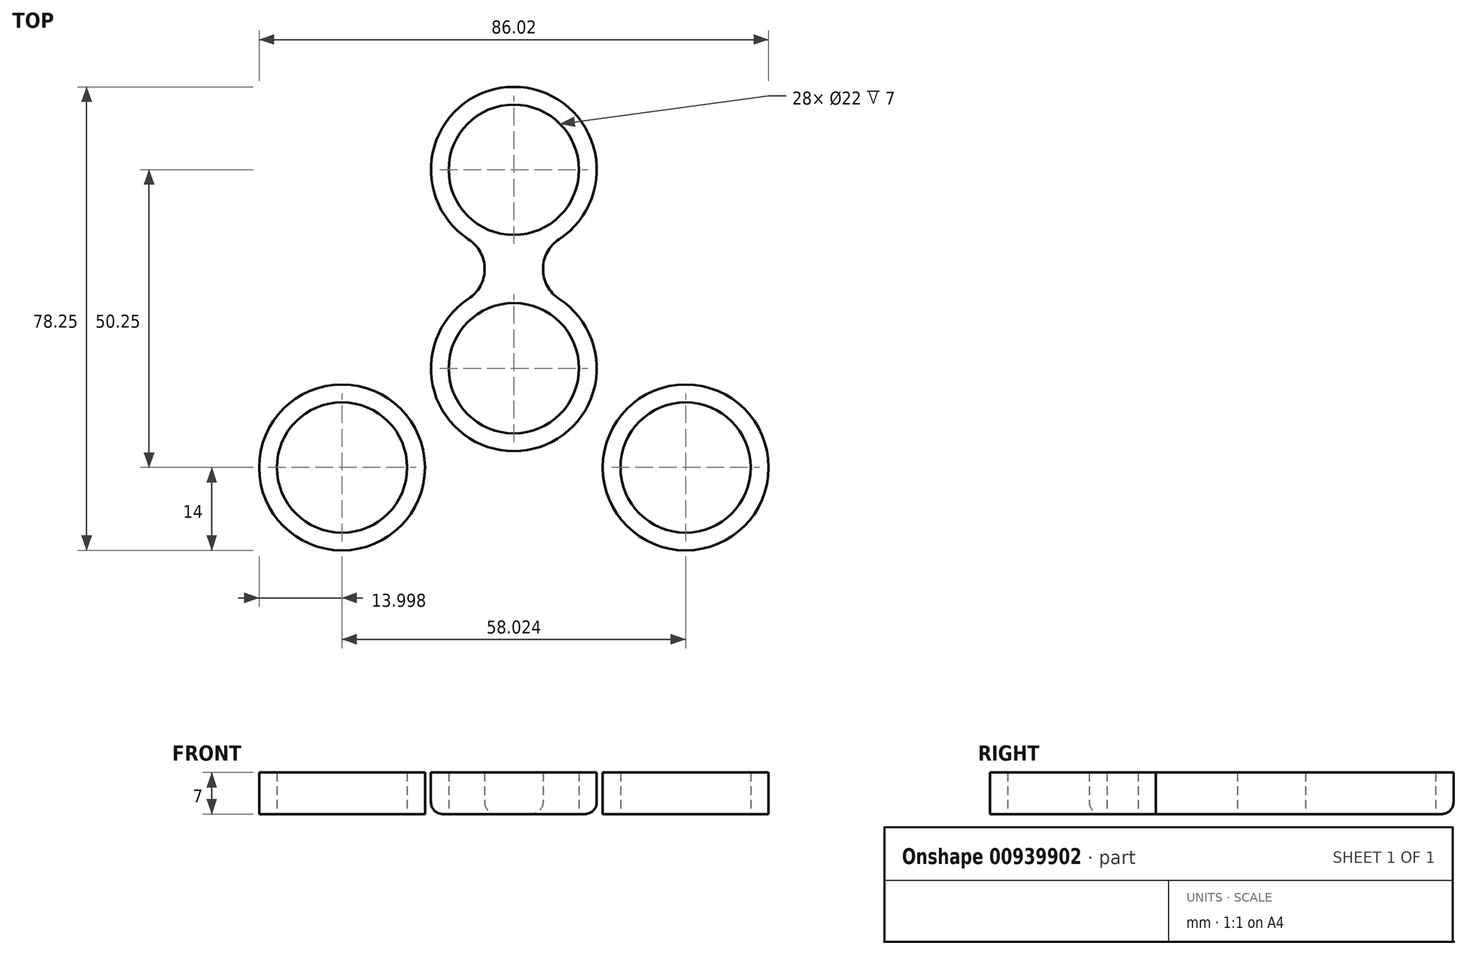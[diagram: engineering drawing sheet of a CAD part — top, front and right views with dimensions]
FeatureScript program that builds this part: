
annotation { "Feature Type Name" : "Feature", "Feature Type Description" : "" }
export const myFeature = defineFeature(function(context is Context, id is Id, definition is map)
    precondition{}
    {
        {
            var Q0;
            Q0=qCreatedBy(makeId("Top.planeOp"),FACE);
            var sketch = newSketch(context, id + "F0", { "sketchPlane" : qUnion([Q0])});
            skCircle(sketch, "E0", {"center": v(0, 0) * mm, "radius": 11 * mm});
            skCircle(sketch, "E1.0", {"center": v(0, 0) * mm, "radius": 14 * mm});
            skCircle(sketch, "E2", {"center": v(0, 0) * mm, "radius": 47.5 * mm, "construction": true});
            skCircle(sketch, "E3", {"center": v(0, 33.5) * mm, "radius": 11 * mm});
            skCircle(sketch, "E4.0", {"center": v(0, 33.5) * mm, "radius": 14 * mm});
            skCircle(sketch, "E5.1.0", {"center": v(-29.01, -16.75) * mm, "radius": 14 * mm});
            skCircle(sketch, "E5.1.1", {"center": v(-29.01, -16.75) * mm, "radius": 11 * mm});
            skCircle(sketch, "E5.2.0", {"center": v(29.01, -16.75) * mm, "radius": 14 * mm});
            skCircle(sketch, "E5.2.1", {"center": v(29.01, -16.75) * mm, "radius": 11 * mm});
            skArc(sketch, "E6", {"start": v(-7.65, 11.72) * mm, "mid": v(-4.93, 16.75) * mm, "end": v(-7.65, 21.78) * mm});
            skLineSegment(sketch, "E7", {"start": v(0, 19.5) * mm, "end": v(0, 14) * mm, "construction": true});
            skArc(sketch, "E8.MirrorCS", {"start": v(7.65, 11.72) * mm, "mid": v(4.93, 16.75) * mm, "end": v(7.65, 21.78) * mm});
            skArc(sketch, "E9.1.0", {"start": v(-13.98, 0.76) * mm, "mid": v(-16.97, -4.1) * mm, "end": v(-22.68, -4.26) * mm});
            skArc(sketch, "E9.1.1", {"start": v(-6.33, -12.49) * mm, "mid": v(-12.04, -12.64) * mm, "end": v(-15.03, -17.51) * mm});
            skArc(sketch, "E9.2.0", {"start": v(6.33, -12.49) * mm, "mid": v(12.04, -12.64) * mm, "end": v(15.03, -17.51) * mm});
            skArc(sketch, "E9.2.1", {"start": v(13.98, 0.76) * mm, "mid": v(16.97, -4.1) * mm, "end": v(22.68, -4.26) * mm});
            skLineSegment(sketch, "E10", {"start": v(58.1, 44) * mm, "end": v(58.1, 19.37) * mm});
            skSolve(sketch);
        }
        {
            var Q0;
            Q0=makeQuery(id+"F0.imprint","IMPRINT",FACE,{"disambiguationData":[TD([[makeQuery(id+"F0.imprint","IMPRINT",EDGE,{"derivedFrom":sQuery(id+"F0.wireOp",EDGE,"E3")}),-1.0]])]});
            var Q1;
            {var subQ0=sQuery(id+"F0.wireOp",EDGE,"E6");Q1=makeQuery(id+"F0.imprint","IMPRINT",FACE,{"disambiguationData":[TD([[makeQuery(id+"F0.imprint","IMPRINT",EDGE,{"derivedFrom":subQ0}),-1.0]])]});}
            var Q2;
            Q2=makeQuery(id+"F0.imprint","IMPRINT",FACE,{"disambiguationData":[TD([[makeQuery(id+"F0.imprint","IMPRINT",EDGE,{"derivedFrom":sQuery(id+"F0.wireOp",EDGE,"E0")}),-1.0]])]});
            var Q3;
            {var subQ0=sQuery(id+"F0.wireOp",EDGE,"E9.1.0");Q3=makeQuery(id+"F0.imprint","IMPRINT",FACE,{"disambiguationData":[TD([[makeQuery(id+"F0.imprint","IMPRINT",EDGE,{"derivedFrom":subQ0}),1.0]])]});}
            var Q4;
            Q4=makeQuery(id+"F0.imprint","IMPRINT",FACE,{"disambiguationData":[TD([[makeQuery(id+"F0.imprint","IMPRINT",EDGE,{"derivedFrom":sQuery(id+"F0.wireOp",EDGE,"E5.1.1")}),-1.0]])]});
            var Q5;
            {var subQ0=sQuery(id+"F0.wireOp",EDGE,"E9.2.0");Q5=makeQuery(id+"F0.imprint","IMPRINT",FACE,{"disambiguationData":[TD([[makeQuery(id+"F0.imprint","IMPRINT",EDGE,{"derivedFrom":subQ0}),1.0]])]});}
            var Q6;
            Q6=makeQuery(id+"F0.imprint","IMPRINT",FACE,{"disambiguationData":[TD([[makeQuery(id+"F0.imprint","IMPRINT",EDGE,{"derivedFrom":sQuery(id+"F0.wireOp",EDGE,"E5.2.1")}),-1.0]])]});
            extrude(context, id + "F1", {"entities" : qUnion([Q0, Q1, Q2, Q3, Q4, Q5, Q6]), "depth" : 7 * mm, "offsetDistance" : 25 * mm});
        }
        {
            var Q0;
            Q0=makeQuery(id+"F1.opExtrude","CAP_EDGE",EDGE,{"disambiguationData":[OSD([sQuery(id+"F0.wireOp",EDGE,"E9.1.1")])],"isStart":false});
            var Q1;
            Q1=makeQuery(id+"F1.opExtrude","CAP_EDGE",EDGE,{"disambiguationData":[OSD([sQuery(id+"F0.wireOp",EDGE,"E4.0")])],"isStart":true});
            fillet(context, id + "F2", {"entities" : qUnion([Q0, Q1]), "radius" : 2 * mm, "tangentPropagation" : true, "allowEdgeOverflow" : false});
        }
    });
